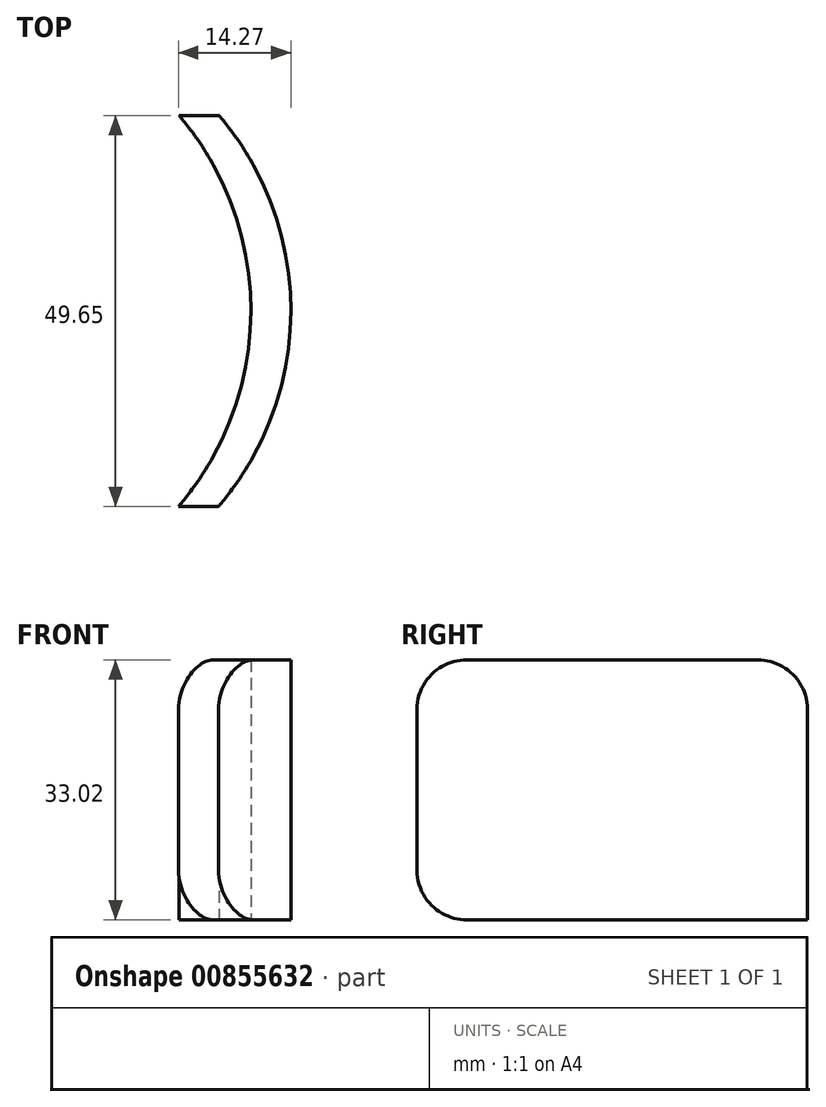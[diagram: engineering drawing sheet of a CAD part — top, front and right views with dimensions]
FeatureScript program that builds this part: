
annotation { "Feature Type Name" : "Feature", "Feature Type Description" : "" }
export const myFeature = defineFeature(function(context is Context, id is Id, definition is map)
    precondition{}
    {
        {
            var Q0;
            Q0=qCreatedBy(makeId("Top.planeOp"),FACE);
            var sketch = newSketch(context, id + "F0", { "sketchPlane" : qUnion([Q0])});
            skCircle(sketch, "E0", {"center": v(0, 0) * mm, "radius": 38.27 * mm});
            skSolve(sketch);
        }
        {
            var Q0;
            Q0=qSketchRegion(id+"F0",true);
            extrude(context, id + "F1", {"entities" : qUnion([Q0]), "depth" : 69.1 * mm, "offsetDistance" : 25.4 * mm});
        }
        {
            var Q0;
            Q0=qCreatedBy(makeId("Right.planeOp"),FACE);
            cPlane(context, id + "F2", {"entities" : qUnion([Q0]), "cplaneType" : CPlaneType.OFFSET, "offset" : 79.25 * mm, "width" : 152.4 * mm, "height" : 152.4 * mm});
        }
        {
            var Q0;
            Q0=qCreatedBy(id+"F2.planeOp",FACE);
            var sketch = newSketch(context, id + "F3", { "sketchPlane" : qUnion([Q0])});
            skLineSegment(sketch, "E1.bottom", {"start": v(-18.53, 51.2) * mm, "end": v(18.42, 51.2) * mm});
            skLineSegment(sketch, "E1.top", {"start": v(-18.53, 18.18) * mm, "end": v(24.77, 18.18) * mm});
            skLineSegment(sketch, "E1.left", {"start": v(-24.88, 44.85) * mm, "end": v(-24.88, 24.53) * mm});
            skLineSegment(sketch, "E1.right", {"start": v(24.77, 44.85) * mm, "end": v(24.77, 18.18) * mm});
            skPoint(sketch, "E2.visualSharp", {"position": v(-24.88, 51.2) * mm});
            skArc(sketch, "E2.filletArc", {"start": v(-18.53, 51.2) * mm, "mid": v(-23.02, 49.34) * mm, "end": v(-24.88, 44.85) * mm});
            skPoint(sketch, "E3.visualSharp", {"position": v(-24.88, 18.18) * mm});
            skArc(sketch, "E3.filletArc", {"start": v(-24.88, 24.53) * mm, "mid": v(-23.02, 20.04) * mm, "end": v(-18.53, 18.18) * mm});
            skPoint(sketch, "E4.visualSharp", {"position": v(24.77, 51.2) * mm});
            skArc(sketch, "E4.filletArc", {"start": v(24.77, 44.85) * mm, "mid": v(22.9, 49.34) * mm, "end": v(18.42, 51.2) * mm});
            skSolve(sketch);
        }
        {
            var Q0;
            Q0=makeQuery(id+"F3.imprint","IMPRINT",FACE,{"disambiguationData":[TD([[makeQuery(id+"F3.imprint","IMPRINT",EDGE,{"derivedFrom":sQuery(id+"F3.wireOp",EDGE,"E1.bottom")}),-1.0]])]});
            var Q1;
            Q1=makeQuery(id+"F1.opExtrude","SWEPT_FACE",FACE,{"disambiguationData":[OSD([sQuery(id+"F0.wireOp",EDGE,"E0")])]});
            var Q2;
            Q2=makeQuery(id+"F1.opExtrude","SWEPT_FACE",FACE,{"disambiguationData":[OSD([sQuery(id+"F0.wireOp",EDGE,"E0")])]});
            extrude(context, id + "F4", {"entities" : qUnion([Q0]), "endBound" : BoundingType.UP_TO_SURFACE, "oppositeDirection" : true, "depth" : 25.4 * mm, "endBoundEntityFace" : qUnion([Q1]), "offsetDistance" : 25.4 * mm, "hasSecondDirection" : true, "secondDirectionBound" : SecondDirectionBoundingType.UP_TO_SURFACE, "secondDirectionOppositeDirection" : true, "secondDirectionDepth" : 25.4 * mm, "secondDirectionBoundEntityFace" : qUnion([Q2]), "hasSecondDirectionOffset" : true, "secondDirectionOffsetDistance" : 5.08 * mm});
        }
        {
            var Q0;
            Q0=makeQuery(id+"F1.opExtrude","SWEPT_BODY",BODY,{"disambiguationData":[OSD([sQuery(id+"F0.wireOp",EDGE,"E0")])]});
            deleteBodies(context, id + "F5", {"entities" : qUnion([Q0])});
        }
    });
